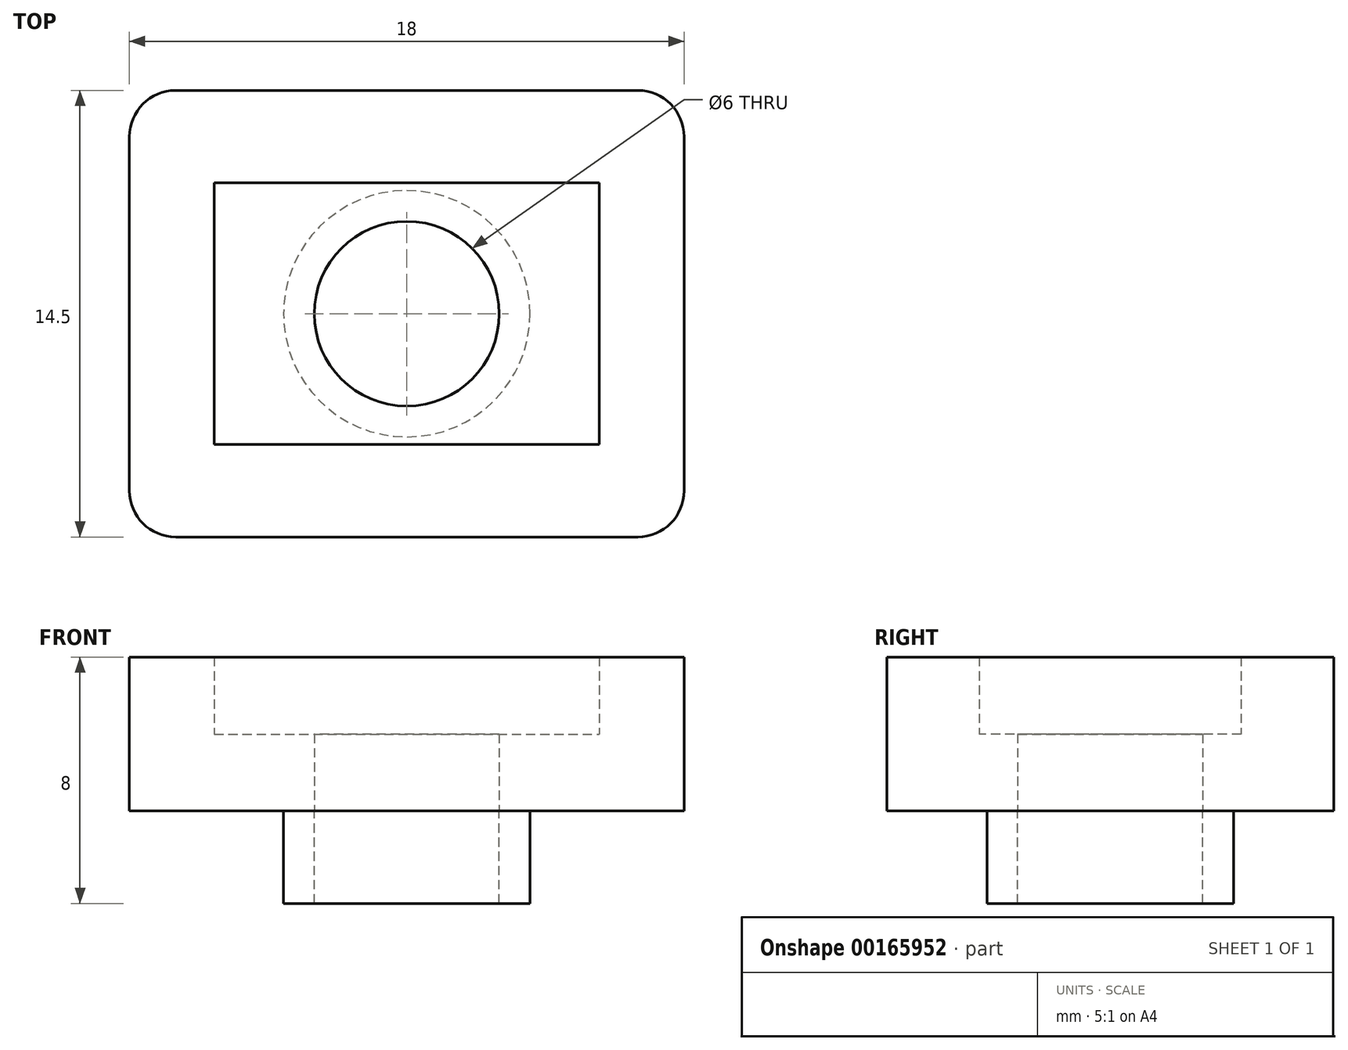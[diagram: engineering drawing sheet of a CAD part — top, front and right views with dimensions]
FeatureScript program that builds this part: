
annotation { "Feature Type Name" : "Feature", "Feature Type Description" : "" }
export const myFeature = defineFeature(function(context is Context, id is Id, definition is map)
    precondition{}
    {
        {
            var Q0;
            Q0=qCreatedBy(makeId("Top.planeOp"),FACE);
            var sketch = newSketch(context, id + "F0", { "sketchPlane" : qUnion([Q0])});
            skLineSegment(sketch, "E0.bottom", {"start": v(-7.5, 7.25) * mm, "end": v(7.5, 7.25) * mm});
            skLineSegment(sketch, "E0.top", {"start": v(-7.5, -7.25) * mm, "end": v(7.5, -7.25) * mm});
            skLineSegment(sketch, "E0.left", {"start": v(-9, 5.75) * mm, "end": v(-9, -5.75) * mm});
            skLineSegment(sketch, "E0.right", {"start": v(9, 5.75) * mm, "end": v(9, -5.75) * mm});
            skLineSegment(sketch, "E1.bottom", {"start": v(-6.25, 4.25) * mm, "end": v(6.25, 4.25) * mm});
            skLineSegment(sketch, "E1.top", {"start": v(-6.25, -4.25) * mm, "end": v(6.25, -4.25) * mm});
            skLineSegment(sketch, "E1.left", {"start": v(-6.25, 4.25) * mm, "end": v(-6.25, -4.25) * mm});
            skLineSegment(sketch, "E1.right", {"start": v(6.25, 4.25) * mm, "end": v(6.25, -4.25) * mm});
            skCircle(sketch, "E2", {"center": v(0, 0) * mm, "radius": 3 * mm});
            skPoint(sketch, "E3.visualSharp", {"position": v(-9, 7.25) * mm});
            skArc(sketch, "E3.filletArc", {"start": v(-7.5, 7.25) * mm, "mid": v(-8.56, 6.81) * mm, "end": v(-9, 5.75) * mm});
            skPoint(sketch, "E4.visualSharp", {"position": v(9, 7.25) * mm});
            skArc(sketch, "E4.filletArc", {"start": v(9, 5.75) * mm, "mid": v(8.56, 6.81) * mm, "end": v(7.5, 7.25) * mm});
            skPoint(sketch, "E5.visualSharp", {"position": v(9, -7.25) * mm});
            skArc(sketch, "E5.filletArc", {"start": v(7.5, -7.25) * mm, "mid": v(8.56, -6.81) * mm, "end": v(9, -5.75) * mm});
            skPoint(sketch, "E6.visualSharp", {"position": v(-9, -7.25) * mm});
            skArc(sketch, "E6.filletArc", {"start": v(-9, -5.75) * mm, "mid": v(-8.56, -6.81) * mm, "end": v(-7.5, -7.25) * mm});
            skCircle(sketch, "E7", {"center": v(0, 0) * mm, "radius": 4 * mm});
            skSolve(sketch);
        }
        {
            var Q0;
            Q0=makeQuery(id+"F0.imprint","IMPRINT",FACE,{"disambiguationData":[TD([[makeQuery(id+"F0.imprint","IMPRINT",EDGE,{"derivedFrom":sQuery(id+"F0.wireOp",EDGE,"E1.bottom")}),-1.0]])]});
            var Q1;
            Q1=makeQuery(id+"F0.imprint","IMPRINT",FACE,{"disambiguationData":[TD([[makeQuery(id+"F0.imprint","IMPRINT",EDGE,{"derivedFrom":sQuery(id+"F0.wireOp",EDGE,"E2")}),-1.0]])]});
            extrude(context, id + "F1", {"entities" : qUnion([Q0, Q1]), "depth" : 2.5 * mm});
        }
        {
            var Q0;
            Q0=qSketchRegion(id+"F0",true);
            extrude(context, id + "F2", {"entities" : qUnion([Q0]), "operationType" : NewBodyOperationType.ADD, "depth" : 5 * mm});
        }
        {
            var Q0;
            Q0=makeQuery(id+"F0.imprint","IMPRINT",FACE,{"disambiguationData":[TD([[makeQuery(id+"F0.imprint","IMPRINT",EDGE,{"derivedFrom":sQuery(id+"F0.wireOp",EDGE,"E2")}),-1.0]])]});
            extrude(context, id + "F3", {"entities" : qUnion([Q0]), "oppositeDirection" : true, "depth" : 3 * mm});
        }
    });
